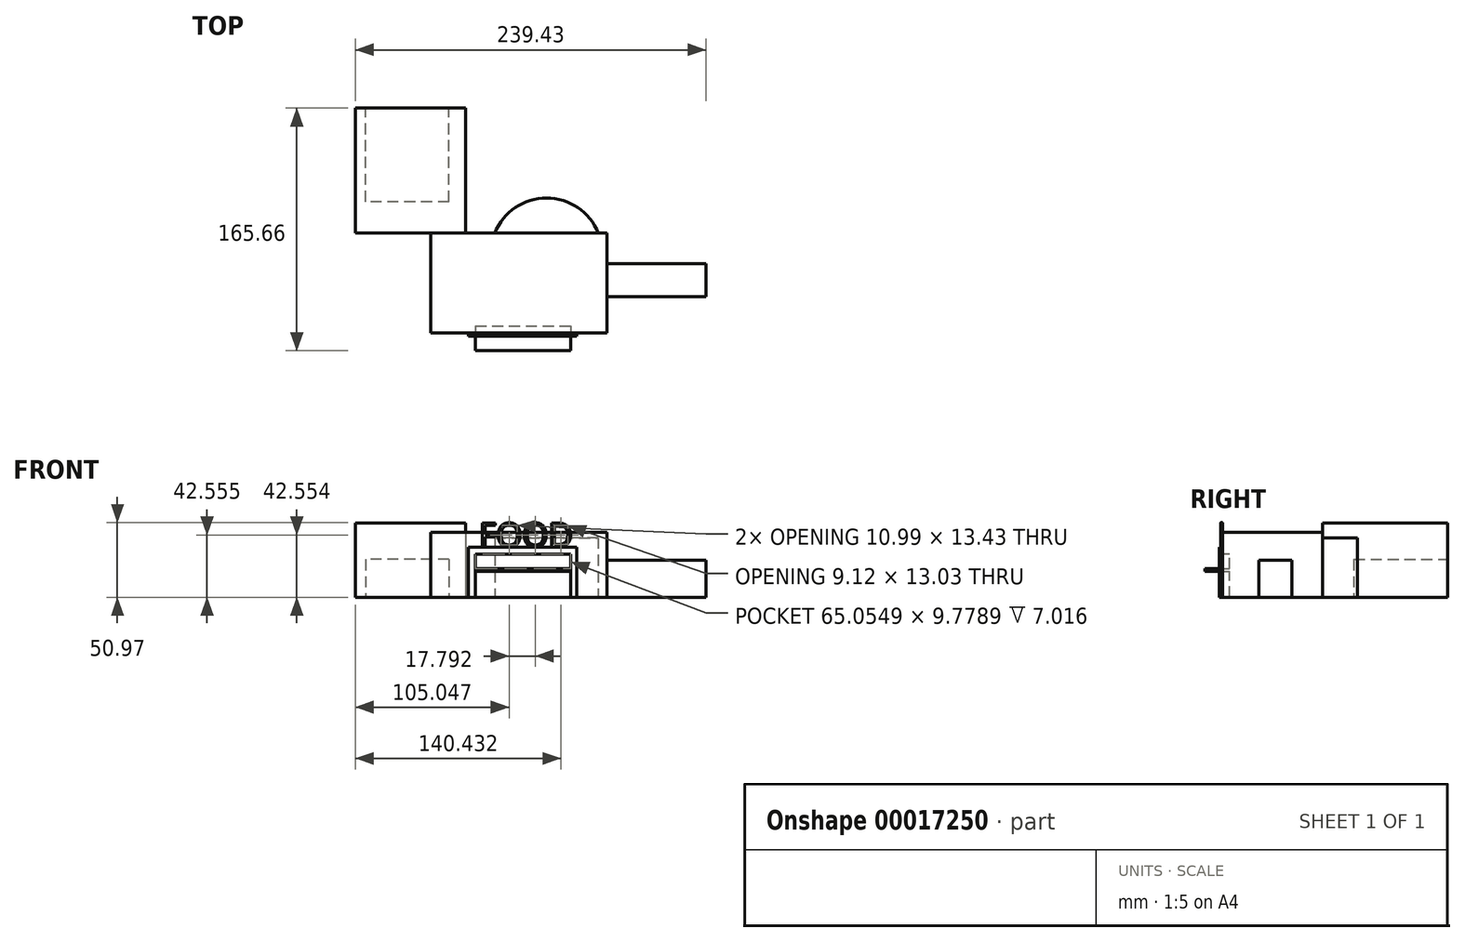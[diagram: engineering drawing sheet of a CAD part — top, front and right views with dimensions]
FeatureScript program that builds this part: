
annotation { "Feature Type Name" : "Feature", "Feature Type Description" : "" }
export const myFeature = defineFeature(function(context is Context, id is Id, definition is map)
    precondition{}
    {
        {
            var Q0;
            Q0=qCreatedBy(makeId("Top.planeOp"),FACE);
            var sketch = newSketch(context, id + "F0", { "sketchPlane" : qUnion([Q0])});
            skLineSegment(sketch, "E0.bottom", {"start": v(-63.8, -10.76) * mm, "end": v(56.54, -10.76) * mm});
            skLineSegment(sketch, "E0.top", {"start": v(-63.8, -79.04) * mm, "end": v(56.54, -79.04) * mm});
            skLineSegment(sketch, "E0.left", {"start": v(-63.8, -10.76) * mm, "end": v(-63.8, -79.04) * mm});
            skLineSegment(sketch, "E0.right", {"start": v(56.54, -10.76) * mm, "end": v(56.54, -79.04) * mm});
            skLineSegment(sketch, "E1.bottom", {"start": v(-39.95, -10.76) * mm, "end": v(-115.37, -10.76) * mm});
            skLineSegment(sketch, "E1.top", {"start": v(-39.95, 74.5) * mm, "end": v(-115.37, 74.5) * mm});
            skLineSegment(sketch, "E1.left", {"start": v(-39.95, -10.76) * mm, "end": v(-39.95, 74.5) * mm});
            skLineSegment(sketch, "E1.right", {"start": v(-115.37, -10.76) * mm, "end": v(-115.37, 74.5) * mm});
            skLineSegment(sketch, "E2.bottom", {"start": v(56.54, -31.63) * mm, "end": v(124.06, -31.63) * mm});
            skLineSegment(sketch, "E2.top", {"start": v(56.54, -54.1) * mm, "end": v(124.06, -54.1) * mm});
            skLineSegment(sketch, "E2.left", {"start": v(56.54, -31.63) * mm, "end": v(56.54, -54.1) * mm});
            skLineSegment(sketch, "E2.right", {"start": v(124.06, -31.63) * mm, "end": v(124.06, -54.1) * mm});
            skArc(sketch, "E3", {"start": v(50.55, -10.76) * mm, "mid": v(15.2, 13.17) * mm, "end": v(-20.16, -10.76) * mm});
            skSolve(sketch);
        }
        {
            var Q0;
            {var subQ2=sQuery(id+"F0.wireOp",EDGE,"E0.top");Q0=makeQuery(id+"F0.imprint","IMPRINT",FACE,{"disambiguationData":[TD([[makeQuery(id+"F0.imprint","IMPRINT",EDGE,{"derivedFrom":subQ2}),1.0]])]});}
            extrude(context, id + "F1", {"entities" : qUnion([Q0]), "depth" : 44.45 * mm});
        }
        {
            var Q0;
            Q0=makeQuery(id+"F0.imprint","IMPRINT",FACE,{"disambiguationData":[TD([[makeQuery(id+"F0.imprint","IMPRINT",EDGE,{"derivedFrom":sQuery(id+"F0.wireOp",EDGE,"E2.bottom")}),-1.0]])]});
            extrude(context, id + "F2", {"entities" : qUnion([Q0]), "operationType" : NewBodyOperationType.ADD, "depth" : 25.4 * mm});
        }
        {
            var Q0;
            Q0=makeQuery(id+"F0.imprint","IMPRINT",FACE,{"disambiguationData":[TD([[makeQuery(id+"F0.imprint","IMPRINT",EDGE,{"derivedFrom":sQuery(id+"F0.wireOp",EDGE,"E1.top")}),1.0]])]});
            extrude(context, id + "F3", {"entities" : qUnion([Q0]), "operationType" : NewBodyOperationType.ADD, "depth" : 50.8 * mm});
        }
        {
            var Q0;
            {var subQ0=sQuery(id+"F0.wireOp",EDGE,"E3");Q0=makeQuery(id+"F0.imprint","IMPRINT",FACE,{"disambiguationData":[TD([[makeQuery(id+"F0.imprint","IMPRINT",EDGE,{"derivedFrom":subQ0}),1.0]])]});}
            extrude(context, id + "F4", {"entities" : qUnion([Q0]), "depth" : 40.64 * mm});
        }
        {
            var Q0;
            Q0=makeQuery(id+"F1.opExtrude","SWEPT_FACE",FACE,{"disambiguationData":[OSD([sQuery(id+"F0.wireOp",EDGE,"E0.top")])]});
            var sketch = newSketch(context, id + "F5", { "sketchPlane" : qUnion([Q0])});
            skLineSegment(sketch, "E4.bottom", {"start": v(-33.41, 0) * mm, "end": v(31.64, 0) * mm});
            skLineSegment(sketch, "E4.top", {"start": v(-33.41, 29.35) * mm, "end": v(31.64, 29.35) * mm});
            skLineSegment(sketch, "E4.left", {"start": v(-33.41, 0) * mm, "end": v(-33.41, 29.35) * mm});
            skLineSegment(sketch, "E4.right", {"start": v(31.64, 0) * mm, "end": v(31.64, 29.35) * mm});
            skSolve(sketch);
        }
        {
            var Q0;
            Q0 = qSketchRegion(id + "F5", true);
            extrude(context, id + "F6", {"entities" : qUnion([Q0]), "operationType" : NewBodyOperationType.REMOVE, "oppositeDirection" : true, "depth" : 4.73 * mm});
        }
        {
            var Q0;
            Q0=makeQuery(id+"F3.opExtrude","SWEPT_FACE",FACE,{"disambiguationData":[OSD([sQuery(id+"F0.wireOp",EDGE,"E1.top")])]});
            var sketch = newSketch(context, id + "F7", { "sketchPlane" : qUnion([Q0])});
            skLineSegment(sketch, "E5.bottom", {"start": v(51.49, 25.84) * mm, "end": v(108.2, 25.84) * mm});
            skLineSegment(sketch, "E5.top", {"start": v(51.49, 0) * mm, "end": v(108.2, 0) * mm});
            skLineSegment(sketch, "E5.left", {"start": v(51.49, 25.84) * mm, "end": v(51.49, 0) * mm});
            skLineSegment(sketch, "E5.right", {"start": v(108.2, 25.84) * mm, "end": v(108.2, 0) * mm});
            skSolve(sketch);
        }
        {
            var Q0;
            Q0 = qSketchRegion(id + "F7", true);
            extrude(context, id + "F8", {"entities" : qUnion([Q0]), "operationType" : NewBodyOperationType.REMOVE, "oppositeDirection" : true, "depth" : 63.83 * mm});
        }
        {
            var Q0;
            Q0=makeQuery(id+"F6.boolean.opBoolean","COPY",FACE,{"derivedFrom":makeQuery(id+"F6.opExtrude","CAP_FACE",FACE,{"disambiguationData":[OSD([sQuery(id+"F5.wireOp",EDGE,"E4.bottom"),sQuery(id+"F5.wireOp",EDGE,"E4.top"),sQuery(id+"F5.wireOp",EDGE,"E4.left"),sQuery(id+"F5.wireOp",EDGE,"E4.right")])],"isStart":false})});
            var sketch = newSketch(context, id + "F9", { "sketchPlane" : qUnion([Q0])});
            skLineSegment(sketch, "E6.bottom", {"start": v(-33.41, 19.57) * mm, "end": v(31.64, 19.57) * mm});
            skLineSegment(sketch, "E6.top", {"start": v(-33.41, 17.7) * mm, "end": v(31.64, 17.7) * mm});
            skLineSegment(sketch, "E6.left", {"start": v(-33.41, 19.57) * mm, "end": v(-33.41, 17.7) * mm});
            skLineSegment(sketch, "E6.right", {"start": v(31.64, 19.57) * mm, "end": v(31.64, 17.7) * mm});
            skSolve(sketch);
        }
        {
            var Q0;
            Q0 = qSketchRegion(id + "F9", true);
            extrude(context, id + "F10", {"entities" : qUnion([Q0]), "depth" : 16.85 * mm});
        }
        {
            var Q0;
            Q0=makeQuery(id+"F1.opExtrude","SWEPT_FACE",FACE,{"disambiguationData":[OSD([sQuery(id+"F0.wireOp",EDGE,"E0.top")])]});
            var sketch = newSketch(context, id + "F11", { "sketchPlane" : qUnion([Q0])});
            skLineSegment(sketch, "E7.bottom", {"start": v(-33.41, 0) * mm, "end": v(-38.09, 0) * mm});
            skLineSegment(sketch, "E7.top", {"start": v(-33.41, 34.4) * mm, "end": v(-38.09, 34.4) * mm});
            skLineSegment(sketch, "E7.left", {"start": v(-33.41, 0) * mm, "end": v(-33.41, 34.4) * mm});
            skLineSegment(sketch, "E7.right", {"start": v(-38.09, 0) * mm, "end": v(-38.09, 34.4) * mm});
            skLineSegment(sketch, "E8.bottom", {"start": v(31.64, 0) * mm, "end": v(35.75, 0) * mm});
            skLineSegment(sketch, "E8.top", {"start": v(31.64, 34.4) * mm, "end": v(35.75, 34.4) * mm});
            skLineSegment(sketch, "E8.left", {"start": v(31.64, 0) * mm, "end": v(31.64, 34.4) * mm});
            skLineSegment(sketch, "E8.right", {"start": v(35.75, 0) * mm, "end": v(35.75, 34.4) * mm});
            skLineSegment(sketch, "E9.bottom", {"start": v(-33.41, 34.4) * mm, "end": v(31.64, 34.4) * mm});
            skLineSegment(sketch, "E9.top", {"start": v(-33.41, 29.35) * mm, "end": v(31.64, 29.35) * mm});
            skLineSegment(sketch, "E9.left", {"start": v(-33.41, 34.4) * mm, "end": v(-33.41, 29.35) * mm});
            skLineSegment(sketch, "E9.right", {"start": v(31.64, 34.4) * mm, "end": v(31.64, 29.35) * mm});
            skSolve(sketch);
        }
        {
            var Q0;
            Q0 = qSketchRegion(id + "F11", true);
            extrude(context, id + "F12", {"entities" : qUnion([Q0]), "operationType" : NewBodyOperationType.ADD, "depth" : 2.3 * mm});
        }
        {
            var Q0;
            Q0=makeQuery(id+"F1.opExtrude","SWEPT_FACE",FACE,{"disambiguationData":[OSD([sQuery(id+"F0.wireOp",EDGE,"E0.top")])]});
            var sketch = newSketch(context, id + "F13", { "sketchPlane" : qUnion([Q0])});
            skText(sketch, "E10", { "text": "FOOD", "fontName": "OpenSans-Regular.ttf"});
            const initialGuessF13  = {"E10": [-0.03101, 0.0344, 1, 0, 0.01645]};
            skSetInitialGuess(sketch, initialGuessF13);
            skSolve(sketch);
        }
        {
            var Q0;
            Q0 = qSketchRegion(id + "F13", true);
            extrude(context, id + "F14", {"entities" : qUnion([Q0]), "depth" : 1.28 * mm});
        }
    });
